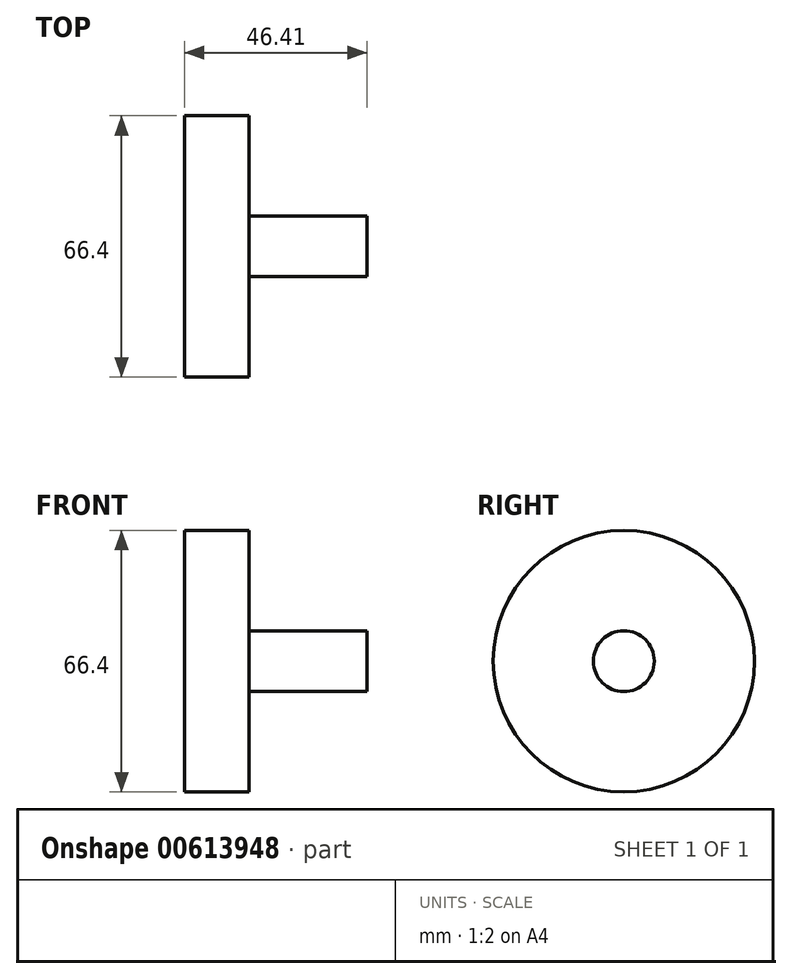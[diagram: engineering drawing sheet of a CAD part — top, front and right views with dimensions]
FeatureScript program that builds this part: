
annotation { "Feature Type Name" : "Feature", "Feature Type Description" : "" }
export const myFeature = defineFeature(function(context is Context, id is Id, definition is map)
    precondition{}
    {
        {
            var Q0;
            Q0=qCreatedBy(makeId("Front.planeOp"),FACE);
            var sketch = newSketch(context, id + "F0", { "sketchPlane" : qUnion([Q0])});
            skLineSegment(sketch, "E0", {"start": v(-113.93, 33.2) * mm, "end": v(-97.56, 33.2) * mm});
            skLineSegment(sketch, "E1", {"start": v(-97.56, 7.73) * mm, "end": v(-67.54, 7.73) * mm});
            skLineSegment(sketch, "E2", {"start": v(-67.54, 7.73) * mm, "end": v(-67.54, 0) * mm});
            skLineSegment(sketch, "E3", {"start": v(-67.54, 0) * mm, "end": v(-113.95, 0) * mm});
            skLineSegment(sketch, "E4", {"start": v(-97.56, 33.2) * mm, "end": v(-97.56, 0) * mm});
            skLineSegment(sketch, "E5", {"start": v(-113.93, 33.2) * mm, "end": v(-113.95, 0) * mm});
            skSolve(sketch);
        }
        {
            var Q0;
            Q0 = qSketchRegion(id + "F0", true);
            var Q1;
            Q1=sQuery(id+"F0.wireOp",EDGE,"E3");
            revolve(context, id + "F1", {"entities" : qUnion([Q0]), "axis" : qUnion([Q1]), "revolveType" : RevolveType.FULL});
        }
    });
